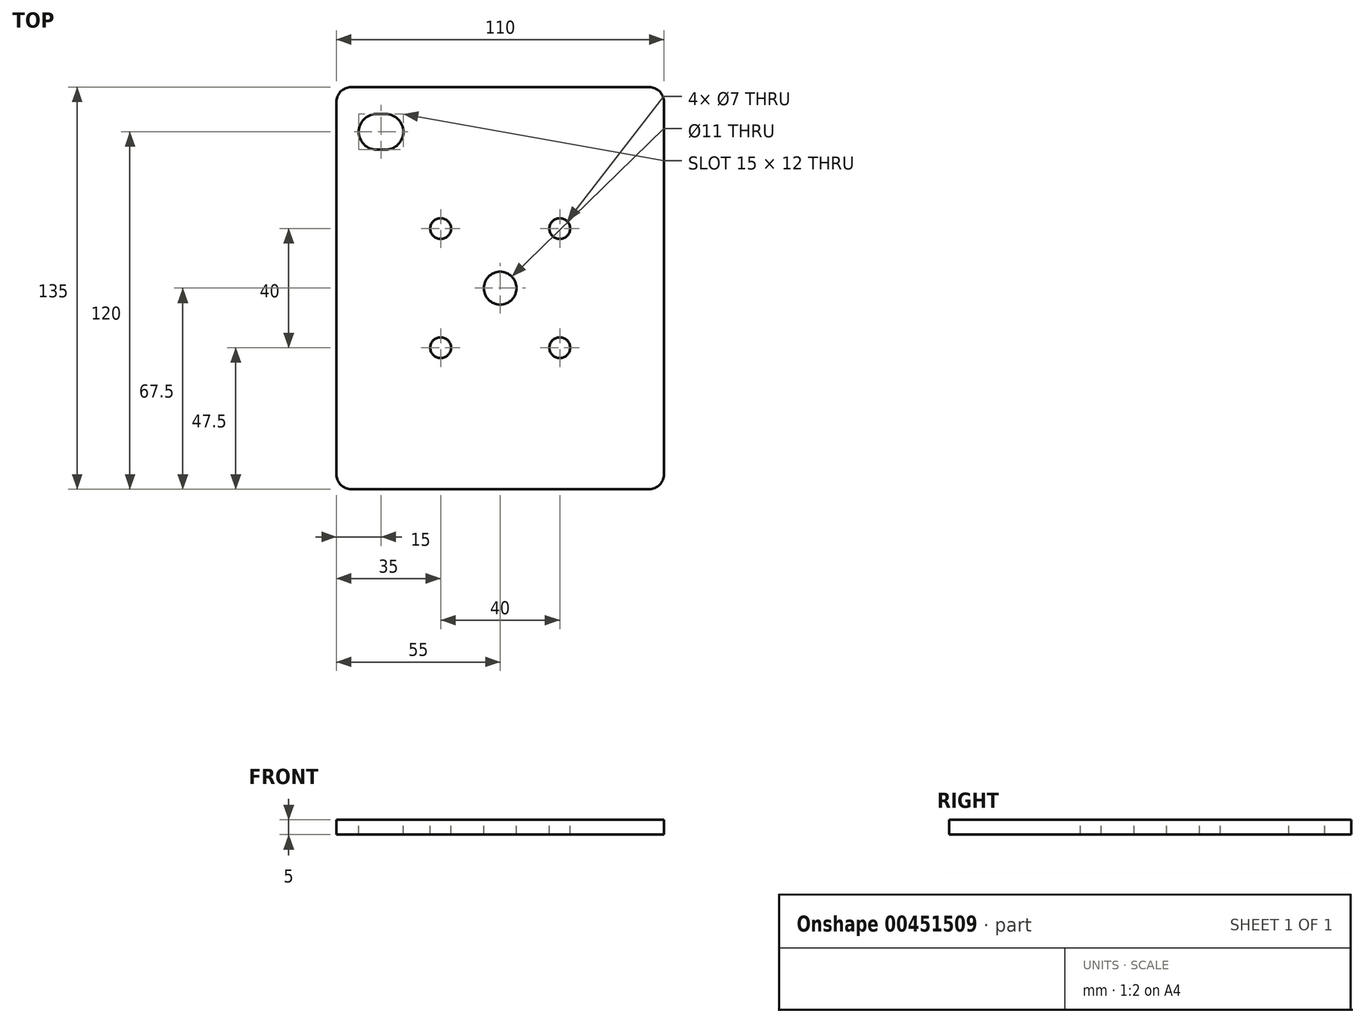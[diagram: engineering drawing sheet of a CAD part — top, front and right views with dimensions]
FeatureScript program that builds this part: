
annotation { "Feature Type Name" : "Feature", "Feature Type Description" : "" }
export const myFeature = defineFeature(function(context is Context, id is Id, definition is map)
    precondition{}
    {
        {
            var Q0;
            Q0=qCreatedBy(makeId("Top.planeOp"),FACE);
            var sketch = newSketch(context, id + "F0", { "sketchPlane" : qUnion([Q0])});
            skLineSegment(sketch, "E0.bottom", {"start": v(55, -67.5) * mm, "end": v(-55, -67.5) * mm});
            skLineSegment(sketch, "E0.top", {"start": v(55, 67.5) * mm, "end": v(-55, 67.5) * mm});
            skLineSegment(sketch, "E0.left", {"start": v(55, -67.5) * mm, "end": v(55, 67.5) * mm});
            skLineSegment(sketch, "E0.right", {"start": v(-55, -67.5) * mm, "end": v(-55, 67.5) * mm});
            skPoint(sketch, "E0.middle", {"position": v(0, 0) * mm});
            skSolve(sketch);
        }
        {
            var Q0;
            Q0=makeQuery(id+"F0.imprint","IMPRINT",FACE,{"disambiguationData":[TD([[makeQuery(id+"F0.imprint","IMPRINT",EDGE,{"derivedFrom":sQuery(id+"F0.wireOp",EDGE,"E0.bottom")}),-1.0]])]});
            extrude(context, id + "F1", {"entities" : qUnion([Q0]), "depth" : 5 * mm});
        }
        {
            var Q0;
            Q0=makeQuery(id+"F1.opExtrude","CAP_FACE",FACE,{"disambiguationData":[OSD([sQuery(id+"F0.wireOp",EDGE,"E0.bottom"),sQuery(id+"F0.wireOp",EDGE,"E0.top"),sQuery(id+"F0.wireOp",EDGE,"E0.left"),sQuery(id+"F0.wireOp",EDGE,"E0.right")])],"isStart":false});
            var sketch = newSketch(context, id + "F2", { "sketchPlane" : qUnion([Q0])});
            skLineSegment(sketch, "E1.bottom", {"start": v(20, -20) * mm, "end": v(-20, -20) * mm, "construction": true});
            skLineSegment(sketch, "E1.top", {"start": v(20, 20) * mm, "end": v(-20, 20) * mm, "construction": true});
            skLineSegment(sketch, "E1.left", {"start": v(20, -20) * mm, "end": v(20, 20) * mm, "construction": true});
            skLineSegment(sketch, "E1.right", {"start": v(-20, -20) * mm, "end": v(-20, 20) * mm, "construction": true});
            skPoint(sketch, "E1.middle", {"position": v(0, 0) * mm});
            skCircle(sketch, "E2", {"center": v(-20, 20) * mm, "radius": 3.5 * mm});
            skCircle(sketch, "E3", {"center": v(20, 20) * mm, "radius": 3.5 * mm});
            skCircle(sketch, "E4", {"center": v(20, -20) * mm, "radius": 3.5 * mm});
            skCircle(sketch, "E5", {"center": v(-20, -20) * mm, "radius": 3.5 * mm});
            skCircle(sketch, "E6", {"center": v(0, 0) * mm, "radius": 5.5 * mm});
            skSolve(sketch);
        }
        {
            var Q0;
            Q0=qSketchRegion(id+"F2",true);
            extrude(context, id + "F3", {"entities" : qUnion([Q0]), "operationType" : NewBodyOperationType.REMOVE, "oppositeDirection" : true, "depth" : 25 * mm});
        }
        {
            var Q0;
            Q0=makeQuery(id+"F1.opExtrude","CAP_FACE",FACE,{"disambiguationData":[OSD([sQuery(id+"F0.wireOp",EDGE,"E0.bottom"),sQuery(id+"F0.wireOp",EDGE,"E0.top"),sQuery(id+"F0.wireOp",EDGE,"E0.left"),sQuery(id+"F0.wireOp",EDGE,"E0.right")])],"isStart":false});
            var sketch = newSketch(context, id + "F4", { "sketchPlane" : qUnion([Q0])});
            skLineSegment(sketch, "E7", {"start": v(-41.5, 52.5) * mm, "end": v(-38.5, 52.5) * mm});
            skArc(sketch, "E8.0.startCap", {"start": v(-41.5, 46.5) * mm, "mid": v(-47.5, 52.5) * mm, "end": v(-41.5, 58.5) * mm});
            skArc(sketch, "E8.0.endCap", {"start": v(-38.5, 58.5) * mm, "mid": v(-32.5, 52.5) * mm, "end": v(-38.5, 46.5) * mm});
            skLineSegment(sketch, "E8.0.left", {"start": v(-41.5, 58.5) * mm, "end": v(-38.5, 58.5) * mm});
            skLineSegment(sketch, "E8.0.right", {"start": v(-41.5, 46.5) * mm, "end": v(-38.5, 46.5) * mm});
            skSolve(sketch);
        }
        {
            var Q0;
            Q0=qSketchRegion(id+"F4",true);
            extrude(context, id + "F5", {"entities" : qUnion([Q0]), "operationType" : NewBodyOperationType.REMOVE, "oppositeDirection" : true, "depth" : 25 * mm});
        }
        {
            var Q0;
            Q0=makeQuery(id+"F1.opExtrude","SWEPT_EDGE",EDGE,{"disambiguationData":[OSD([sQuery(id+"F0.wireOp",EDGE,"E0.top"),sQuery(id+"F0.wireOp",EDGE,"E0.right")])]});
            var Q1;
            Q1=makeQuery(id+"F1.opExtrude","SWEPT_EDGE",EDGE,{"disambiguationData":[OSD([sQuery(id+"F0.wireOp",EDGE,"E0.top"),sQuery(id+"F0.wireOp",EDGE,"E0.left")])]});
            var Q2;
            Q2=makeQuery(id+"F1.opExtrude","SWEPT_EDGE",EDGE,{"disambiguationData":[OSD([sQuery(id+"F0.wireOp",EDGE,"E0.bottom"),sQuery(id+"F0.wireOp",EDGE,"E0.left")])]});
            var Q3;
            Q3=makeQuery(id+"F1.opExtrude","SWEPT_EDGE",EDGE,{"disambiguationData":[OSD([sQuery(id+"F0.wireOp",EDGE,"E0.bottom"),sQuery(id+"F0.wireOp",EDGE,"E0.right")])]});
            fillet(context, id + "F6", {"entities" : qUnion([Q0, Q1, Q2, Q3]), "radius" : 5 * mm, "tangentPropagation" : true, "allowEdgeOverflow" : false});
        }
    });
